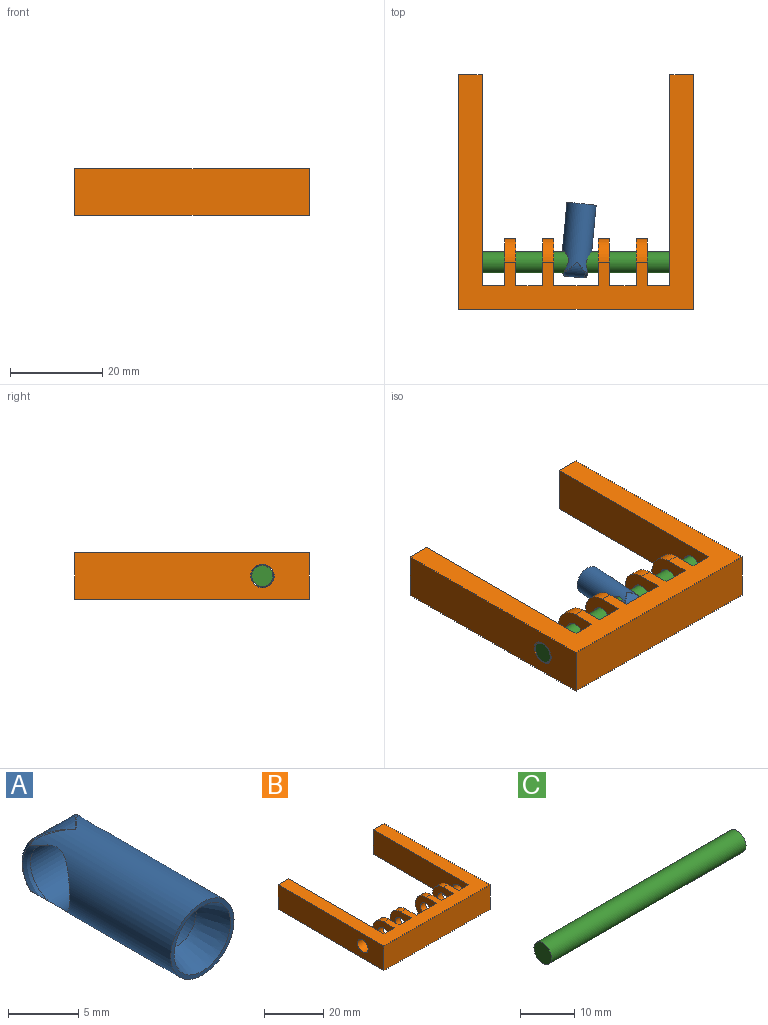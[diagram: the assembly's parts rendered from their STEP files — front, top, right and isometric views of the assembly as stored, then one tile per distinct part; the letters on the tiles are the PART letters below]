
ASSEMBLY  parts=3 mates=2
PART A: 20 faces, bbox 6.4x16.1x6.4 mm
  f0: plane 6.35x6.35mm, normal (0,-1,0), area 6.5mm2, adj f3,f19
  f1: cylinder r=2.54mm len=6.35mm, axis (-1,0,0), area 73.4mm2, adj f3,f5,f7
  f2: cylinder r=3.17mm len=6.35mm, axis (-1,0,0), area 30.6mm2, adj f4,f6,f9,f11,f13,f15
  f3: cylinder r=3.17mm len=14.74mm, axis (0,-1,0), area 240.3mm2, adj f0,f1,f5,f7,f8,f9,f10,f11
  f4: torus R=2.67mm, axis (1,0,0), area 2.8mm2, adj f2,f5,f8,f10
  f5: torus R=3.05mm, axis (1,0,0), area 3.2mm2, adj f1,f3,f4,f8,f10
  f6: torus R=2.67mm, axis (1,0,0), area 2.8mm2, adj f2,f7,f12,f14
  f7: torus R=3.05mm, axis (1,0,0), area 3.2mm2, adj f1,f3,f6,f12,f14
  f8: bspline ~0.6x0.59mm, area 0.1mm2, adj f3,f4,f5,f9
  f9: bspline ~2.32x2.32mm, area 0.3mm2, adj f2,f3,f8
  f10: bspline ~0.6x0.59mm, area 0.1mm2, adj f3,f4,f5,f11
  f11: bspline ~2.32x2.32mm, area 0.3mm2, adj f2,f3,f10
  f12: bspline ~0.58x0.56mm, area 0.1mm2, adj f3,f6,f7,f13
  f13: bspline ~2.32x2.32mm, area 0.3mm2, adj f2,f3,f12
  f14: bspline ~0.58x0.56mm, area 0.1mm2, adj f3,f6,f7,f15
  f15: bspline ~2.32x2.32mm, area 0.4mm2, adj f2,f3,f14
  f16: plane 4.57x4.57mm, normal (0,1,0), area 5mm2, adj f17,f19
  f17: cylinder r=2.29mm len=4.57mm, axis (0,1,0), area 36.5mm2, adj f16,f18
  f18: plane 4.57x4.57mm, normal (0,-1,0), area 16.4mm2, adj f17
  f19: cone r=1.91mm half-angle=20deg, axis (0,-1,0), area 40.2mm2, adj f0,f16
PART B: 32 faces, bbox 50.8x50.8x10.2 mm
  f0: plane 10.16x5.84mm, normal (0,1,0), area 59.3mm2, adj f12,f13,f19,f21
  f1: plane 10.16x4.85mm, normal (0,1,0), area 49.3mm2, adj f10,f12,f13,f18
  f2: plane 10.16x5.84mm, normal (0,1,0), area 59.3mm2, adj f12,f13,f15,f17
  f3: plane 10.16x9.7mm, normal (0,1,0), area 98.5mm2, adj f12,f13,f14,f20
  f4: plane 50.8x10.16mm, normal (-1,0,0), area 495.9mm2, adj f5,f11,f12,f13,f30
  f5: plane 50.8x10.16mm, normal (0,-1,0), area 516.1mm2, adj f4,f6,f12,f13
  f6: plane 50.8x10.16mm, normal (1,0,0), area 495.9mm2, adj f5,f7,f12,f13,f31
  f7: plane 10.16x5.08mm, normal (0,1,0), area 51.6mm2, adj f6,f8,f12,f13
  f8: plane 45.72x10.16mm, normal (-1,0,0), area 444.2mm2, adj f7,f9,f12,f13,f31
  f9: plane 10.16x4.85mm, normal (0,1,0), area 49.3mm2, adj f8,f12,f13,f16
  f10: plane 45.72x10.16mm, normal (1,0,0), area 444.2mm2, adj f1,f11,f12,f13,f30
  f11: plane 10.16x5.08mm, normal (0,1,0), area 51.6mm2, adj f4,f10,f12,f13
  f12: plane 50.8x50.8mm, normal (0,0,1), area 771.2mm2, adj f0,f1,f2,f3,f4,f5,f6,f7
  f13: plane 50.8x50.8mm, normal (0,0,-1), area 771.2mm2, adj f0,f1,f2,f3,f4,f5,f6,f7
  f14: plane 10.16x10.16mm, normal (-1,0,0), area 71.9mm2, adj f3,f12,f13,f24,f29
  f15: plane 10.16x10.16mm, normal (1,0,0), area 71.9mm2, adj f2,f12,f13,f24,f29
  f16: plane 10.16x10.16mm, normal (1,0,0), area 71.9mm2, adj f9,f12,f13,f25,f28
  f17: plane 10.16x10.16mm, normal (-1,0,0), area 71.9mm2, adj f2,f12,f13,f25,f28
  f18: plane 10.16x10.16mm, normal (-1,0,0), area 71.9mm2, adj f1,f12,f13,f23,f27
  f19: plane 10.16x10.16mm, normal (1,0,0), area 71.9mm2, adj f0,f12,f13,f23,f27
  f20: plane 10.16x10.16mm, normal (1,0,0), area 71.9mm2, adj f3,f12,f13,f22,f26
  f21: plane 10.16x10.16mm, normal (-1,0,0), area 71.9mm2, adj f0,f12,f13,f22,f26
  f22: cylinder r=5.08mm len=10.16mm, axis (1,0,0), area 38.2mm2, adj f12,f13,f20,f21
  f23: cylinder r=5.08mm len=10.16mm, axis (-1,0,0), area 38.2mm2, adj f12,f13,f18,f19
  f24: cylinder r=5.08mm len=10.16mm, axis (-1,0,0), area 38.2mm2, adj f12,f13,f14,f15
  f25: cylinder r=5.08mm len=10.16mm, axis (1,0,0), area 38.2mm2, adj f12,f13,f16,f17
  f26: cylinder r=2.54mm len=5.08mm, axis (-1,0,0), area 38.2mm2, adj f20,f21
  f27: cylinder r=2.54mm len=5.08mm, axis (-1,0,0), area 38.2mm2, adj f18,f19
  f28: cylinder r=2.54mm len=5.08mm, axis (-1,0,0), area 38.2mm2, adj f16,f17
  f29: cylinder r=2.54mm len=5.08mm, axis (-1,0,0), area 38.2mm2, adj f14,f15
  f30: cylinder r=2.54mm len=5.08mm, axis (-1,0,0), area 81.1mm2, adj f4,f10
  f31: cylinder r=2.54mm len=5.08mm, axis (-1,0,0), area 81.1mm2, adj f6,f8
PART C: 3 faces, bbox 50.8x4.6x4.6 mm
  f0: cylinder r=2.29mm len=50.8mm, axis (-1,0,0), area 729.7mm2, adj f1,f2
  f1: plane 4.57x4.57mm, normal (1,0,0), area 16.4mm2, adj f0
  f2: plane 4.57x4.57mm, normal (-1,0,0), area 16.4mm2, adj f0
PLACE A rot(axis=(1,-0.05,-0.05),178.8deg) t=(-1.53,33.36,31.42)mm
PLACE B t=(8.52,46.53,26.07)mm fixed
PLACE C t=(-24.42,3.18,2.8)mm
MATE ball A.f1 <-> C.f0  axis (-0.99,0.1,0.11) through (0.98,33.11,31.15)mm
MATE revolute B.f22 <-> C.f0  axis (-1,0,0) through (-24.42,33.11,31.15)mm
